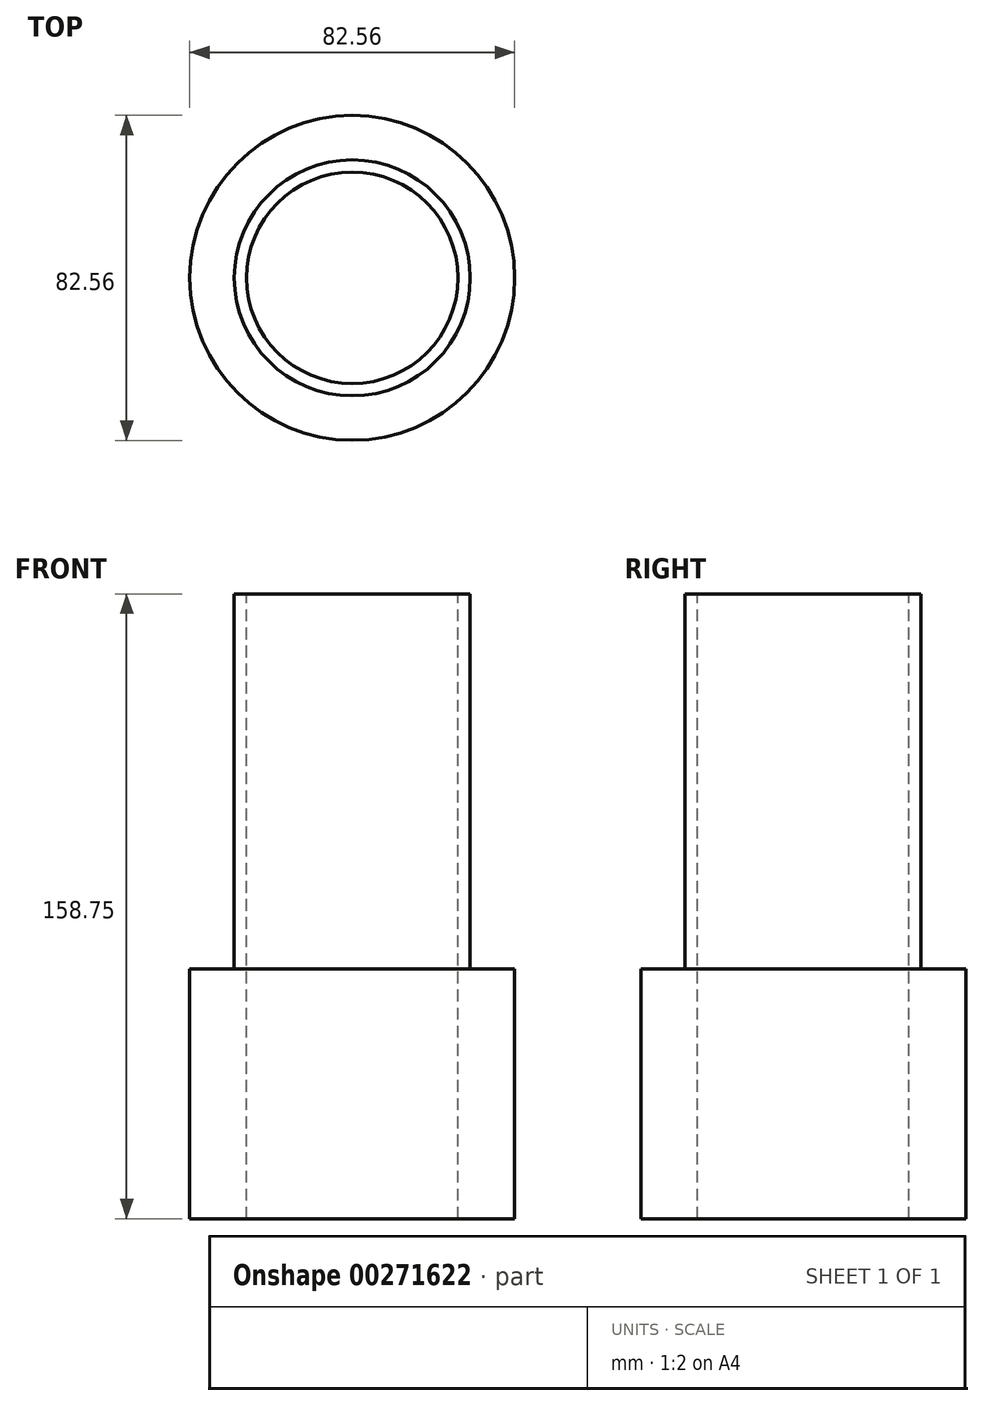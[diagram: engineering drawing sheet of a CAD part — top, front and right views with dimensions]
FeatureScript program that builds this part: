
annotation { "Feature Type Name" : "Feature", "Feature Type Description" : "" }
export const myFeature = defineFeature(function(context is Context, id is Id, definition is map)
    precondition{}
    {
        {
            var Q0;
            Q0=qCreatedBy(makeId("Top.planeOp"),FACE);
            var sketch = newSketch(context, id + "F0", { "sketchPlane" : qUnion([Q0])});
            skCircle(sketch, "E0", {"center": v(0, 0) * mm, "radius": 41.28 * mm});
            skSolve(sketch);
        }
        {
            var Q0;
            Q0=makeQuery(id+"F0.imprint","IMPRINT",FACE,{"disambiguationData":[TD([[makeQuery(id+"F0.imprint","IMPRINT",EDGE,{"derivedFrom":sQuery(id+"F0.wireOp",EDGE,"E0")}),1.0]])]});
            extrude(context, id + "F1", {"entities" : qUnion([Q0]), "depth" : 158.75 * mm});
        }
        {
            var Q0;
            Q0=makeQuery(id+"F1.opExtrude","CAP_FACE",FACE,{"disambiguationData":[OSD([sQuery(id+"F0.wireOp",EDGE,"E0")])],"isStart":false});
            var sketch = newSketch(context, id + "F2", { "sketchPlane" : qUnion([Q0])});
            skCircle(sketch, "E1", {"center": v(0, 0) * mm, "radius": 29.97 * mm});
            skSolve(sketch);
        }
        {
            var Q0;
            Q0=makeQuery(id+"F2.imprint","IMPRINT",FACE,{"disambiguationData":[TD([[makeQuery(id+"F2.imprint","IMPRINT",EDGE,{"derivedFrom":sQuery(id+"F2.wireOp",EDGE,"E1")}),-1.0]])]});
            extrude(context, id + "F3", {"entities" : qUnion([Q0]), "operationType" : NewBodyOperationType.REMOVE, "oppositeDirection" : true, "depth" : 95.25 * mm});
        }
        {
            var Q0;
            Q0=makeQuery(id+"F1.opExtrude","CAP_FACE",FACE,{"disambiguationData":[OSD([sQuery(id+"F0.wireOp",EDGE,"E0")])],"isStart":false});
            var sketch = newSketch(context, id + "F4", { "sketchPlane" : qUnion([Q0])});
            skCircle(sketch, "E2", {"center": v(0, 0) * mm, "radius": 26.86 * mm});
            skSolve(sketch);
        }
        {
            var Q0;
            Q0=makeQuery(id+"F4.imprint","IMPRINT",FACE,{"disambiguationData":[TD([[makeQuery(id+"F4.imprint","IMPRINT",EDGE,{"derivedFrom":sQuery(id+"F4.wireOp",EDGE,"E2")}),1.0]])]});
            extrude(context, id + "F5", {"entities" : qUnion([Q0]), "operationType" : NewBodyOperationType.REMOVE, "endBound" : BoundingType.THROUGH_ALL, "oppositeDirection" : true, "depth" : 25.4 * mm});
        }
    });
